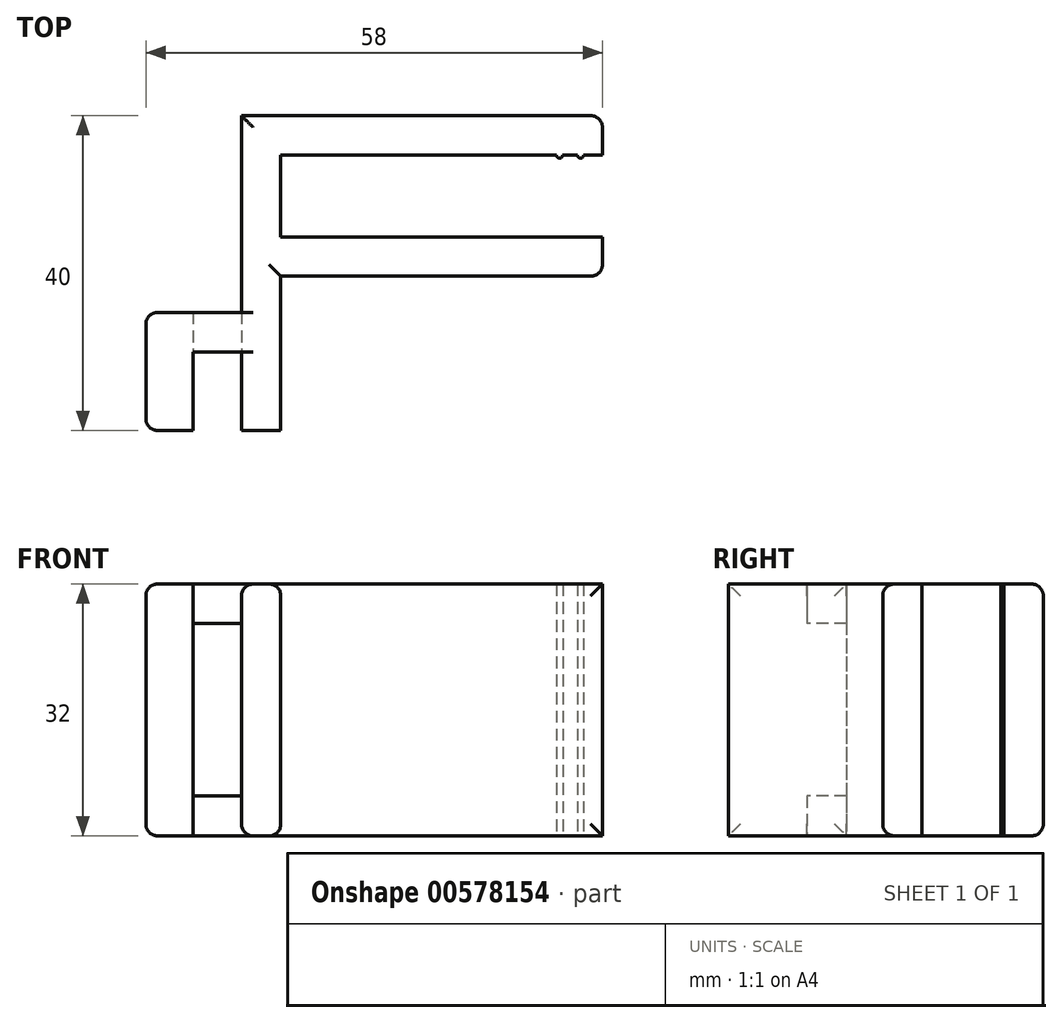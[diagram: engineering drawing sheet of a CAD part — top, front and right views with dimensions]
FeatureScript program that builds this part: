
annotation { "Feature Type Name" : "Feature", "Feature Type Description" : "" }
export const myFeature = defineFeature(function(context is Context, id is Id, definition is map)
    precondition{}
    {
        {
            var Q0;
            Q0=qCreatedBy(makeId("Top.planeOp"),FACE);
            var sketch = newSketch(context, id + "F0", { "sketchPlane" : qUnion([Q0])});
            skLineSegment(sketch, "E0.bottom", {"start": v(0, 0) * mm, "end": v(6, 0) * mm});
            skLineSegment(sketch, "E0.top", {"start": v(12.14, 40) * mm, "end": v(58, 40) * mm});
            skLineSegment(sketch, "E0.left", {"start": v(0, 0) * mm, "end": v(0, 15) * mm});
            skLineSegment(sketch, "E0.right", {"start": v(58, 25) * mm, "end": v(58, 30) * mm});
            skLineSegment(sketch, "E1", {"start": v(58, 35) * mm, "end": v(17.14, 35) * mm});
            skLineSegment(sketch, "E2", {"start": v(58, 25) * mm, "end": v(17.14, 25) * mm});
            skLineSegment(sketch, "E3", {"start": v(6, 0) * mm, "end": v(6, 15) * mm});
            skLineSegment(sketch, "E4", {"start": v(12.14, 0) * mm, "end": v(12.14, 25) * mm});
            skLineSegment(sketch, "E5", {"start": v(17.14, 0) * mm, "end": v(17.14, 25) * mm});
            skLineSegment(sketch, "E6", {"start": v(6, 10) * mm, "end": v(12.14, 10) * mm});
            skLineSegment(sketch, "E7", {"start": v(0, 15) * mm, "end": v(12.14, 15) * mm});
            skLineSegment(sketch, "E8", {"start": v(17.14, 30) * mm, "end": v(17.14, 35) * mm});
            skLineSegment(sketch, "E9", {"start": v(12.14, 25) * mm, "end": v(12.14, 40) * mm});
            skLineSegment(sketch, "E10.trimOffspring", {"start": v(12.14, 0) * mm, "end": v(17.14, 0) * mm});
            skLineSegment(sketch, "E11.trimOffspring", {"start": v(17.14, 30) * mm, "end": v(58, 30) * mm});
            skPoint(sketch, "E12.start.orphan", {"position": v(0, 30) * mm});
            skPoint(sketch, "E13.start.orphan", {"position": v(60.37, 35) * mm});
            skPoint(sketch, "E14.end.orphan", {"position": v(60.37, 40) * mm});
            skPoint(sketch, "E15.start.orphan", {"position": v(60.37, 30) * mm});
            skLineSegment(sketch, "E16.trimOffspring", {"start": v(58, 35) * mm, "end": v(58, 40) * mm});
            skArc(sketch, "E17", {"start": v(52.16, 35) * mm, "mid": v(52.56, 34.6) * mm, "end": v(52.96, 35) * mm});
            skArc(sketch, "E18", {"start": v(54.82, 35) * mm, "mid": v(55.22, 34.6) * mm, "end": v(55.62, 35) * mm});
            skSolve(sketch);
        }
        {
            var Q0;
            Q0 = qSketchRegion(id + "F0", true);
            extrude(context, id + "F1", {"entities" : qUnion([Q0]), "depth" : 32 * mm, "offsetDistance" : 25 * mm});
        }
        {
            var Q0;
            Q0=makeQuery(id+"F1.opExtrude","SWEPT_FACE",FACE,{"disambiguationData":[OSD([sQuery(id+"F0.wireOp",EDGE,"E6")])]});
            var sketch = newSketch(context, id + "F2", { "sketchPlane" : qUnion([Q0])});
            skLineSegment(sketch, "E19.bottom", {"start": v(6, 0) * mm, "end": v(12.14, 0) * mm});
            skLineSegment(sketch, "E19.top", {"start": v(6, 5.07) * mm, "end": v(12.14, 5.07) * mm});
            skLineSegment(sketch, "E19.left", {"start": v(6, 0) * mm, "end": v(6, 5.07) * mm});
            skLineSegment(sketch, "E19.right", {"start": v(12.14, 0) * mm, "end": v(12.14, 5.07) * mm});
            skLineSegment(sketch, "E20.bottom", {"start": v(6, 32) * mm, "end": v(12.14, 32) * mm});
            skLineSegment(sketch, "E20.top", {"start": v(6, 27) * mm, "end": v(12.14, 27) * mm});
            skLineSegment(sketch, "E20.left", {"start": v(6, 32) * mm, "end": v(6, 27) * mm});
            skLineSegment(sketch, "E20.right", {"start": v(12.14, 32) * mm, "end": v(12.14, 27) * mm});
            skSolve(sketch);
        }
        {
            var Q0;
            {var subQ0=sQuery(id+"F2.wireOp",EDGE,"E19.top");Q0=makeQuery(id+"F2.imprint","IMPRINT",FACE,{"disambiguationData":[TD([[makeQuery(id+"F2.imprint","IMPRINT",EDGE,{"derivedFrom":subQ0}),1.0]])]});}
            extrude(context, id + "F3", {"entities" : qUnion([Q0]), "operationType" : NewBodyOperationType.REMOVE, "oppositeDirection" : true, "depth" : 5 * mm, "offsetDistance" : 25 * mm});
        }
        {
            var Q0;
            Q0=makeQuery(id+"F1.opExtrude","SWEPT_FACE",FACE,{"disambiguationData":[OSD([sQuery(id+"F0.wireOp",EDGE,"E2")])]});
            extrude(context, id + "F4", {"entities" : qUnion([Q0]), "operationType" : NewBodyOperationType.ADD, "depth" : 5.4 * mm, "offsetDistance" : 25 * mm});
        }
        {
            var Q0;
            Q0=makeQuery(id+"F1.opExtrude","SWEPT_FACE",FACE,{"disambiguationData":[OSD([sQuery(id+"F0.wireOp",EDGE,"E11.trimOffspring")])]});
            extrude(context, id + "F5", {"entities" : qUnion([Q0]), "operationType" : NewBodyOperationType.REMOVE, "oppositeDirection" : true, "depth" : 5.4 * mm, "offsetDistance" : 25 * mm});
        }
        {
            var Q0;
            Q0=makeQuery(id+"F1.opExtrude","CAP_EDGE",EDGE,{"disambiguationData":[OSD([sQuery(id+"F0.wireOp",EDGE,"E4"),sQuery(id+"F0.wireOp",EDGE,"E9")])],"isStart":false});
            var Q1;
            Q1=makeQuery(id+"F1.opExtrude","CAP_EDGE",EDGE,{"disambiguationData":[OSD([sQuery(id+"F0.wireOp",EDGE,"E4"),sQuery(id+"F0.wireOp",EDGE,"E9")])],"isStart":true});
            var Q2;
            Q2=makeQuery(id+"F1.opExtrude","CAP_EDGE",EDGE,{"disambiguationData":[OSD([sQuery(id+"F0.wireOp",EDGE,"E4")])],"isStart":true});
            var Q3;
            Q3=makeQuery(id+"F1.opExtrude","SWEPT_FACE",FACE,{"disambiguationData":[OSD([sQuery(id+"F0.wireOp",EDGE,"E0.left")])]});
            var Q4;
            Q4=makeQuery(id+"F1.opExtrude","CAP_EDGE",EDGE,{"disambiguationData":[OSD([sQuery(id+"F0.wireOp",EDGE,"E4")])],"isStart":false});
            var Q5;
            Q5=makeQuery(id+"F1.opExtrude","CAP_EDGE",EDGE,{"disambiguationData":[OSD([sQuery(id+"F0.wireOp",EDGE,"E5")])],"isStart":true});
            var Q6;
            {var subQ0=sQuery(id+"F0.wireOp",EDGE,"E11.trimOffspring");var subQ1=sQuery(id+"F0.wireOp",EDGE,"E8");Q6=makeQuery(id+"F5.boolean.opBoolean","MERGE",EDGE,{"derivedFrom":[makeQuery(id+"F1.opExtrude","CAP_EDGE",EDGE,{"disambiguationData":[OSD([subQ1])],"isStart":true}),makeQuery(id+"F5.opExtrude","SWEPT_EDGE",EDGE,{"disambiguationData":[OSD([subQ1,subQ0]),TDD([makeQuery(id+"F1.opExtrude","CAP_VERTEX",VERTEX,{"disambiguationData":[OSD([subQ1,subQ0])],"isStart":true})])]})]});}
            var Q7;
            {var subQ0=sQuery(id+"F0.wireOp",EDGE,"E11.trimOffspring");var subQ1=sQuery(id+"F0.wireOp",EDGE,"E8");Q7=makeQuery(id+"F5.boolean.opBoolean","MERGE",EDGE,{"derivedFrom":[makeQuery(id+"F1.opExtrude","CAP_EDGE",EDGE,{"disambiguationData":[OSD([subQ1])],"isStart":false}),makeQuery(id+"F5.opExtrude","SWEPT_EDGE",EDGE,{"disambiguationData":[OSD([subQ1,subQ0]),TDD([makeQuery(id+"F1.opExtrude","CAP_VERTEX",VERTEX,{"disambiguationData":[OSD([subQ1,subQ0])],"isStart":false})])]})]});}
            var Q8;
            Q8=makeQuery(id+"F1.opExtrude","CAP_EDGE",EDGE,{"disambiguationData":[OSD([sQuery(id+"F0.wireOp",EDGE,"E5")])],"isStart":false});
            var Q9;
            {var subQ0=sQuery(id+"F0.wireOp",EDGE,"E2");Q9=makeQuery(id+"F4.opExtrude","CAP_EDGE",EDGE,{"disambiguationData":[OSD([subQ0]),TDD([makeQuery(id+"F1.opExtrude","CAP_EDGE",EDGE,{"disambiguationData":[OSD([subQ0])],"isStart":false})])],"isStart":false});}
            var Q10;
            {var subQ0=sQuery(id+"F0.wireOp",EDGE,"E2");Q10=makeQuery(id+"F4.opExtrude","CAP_EDGE",EDGE,{"disambiguationData":[OSD([subQ0]),TDD([makeQuery(id+"F1.opExtrude","CAP_EDGE",EDGE,{"disambiguationData":[OSD([subQ0])],"isStart":true})])],"isStart":false});}
            var Q11;
            Q11=makeQuery(id+"F1.opExtrude","CAP_EDGE",EDGE,{"disambiguationData":[OSD([sQuery(id+"F0.wireOp",EDGE,"E0.top")])],"isStart":true});
            var Q12;
            Q12=makeQuery(id+"F1.opExtrude","CAP_EDGE",EDGE,{"disambiguationData":[OSD([sQuery(id+"F0.wireOp",EDGE,"E0.top")])],"isStart":false});
            var Q13;
            Q13=makeQuery(id+"F1.opExtrude","SWEPT_EDGE",EDGE,{"disambiguationData":[OSD([sQuery(id+"F0.wireOp",EDGE,"E0.top"),sQuery(id+"F0.wireOp",EDGE,"E16.trimOffspring")])]});
            var Q14;
            Q14=makeQuery(id+"F4.opExtrude","CAP_EDGE",EDGE,{"disambiguationData":[OSD([sQuery(id+"F0.wireOp",EDGE,"E0.right"),sQuery(id+"F0.wireOp",EDGE,"E2")])],"isStart":false});
            fillet(context, id + "F6", {"entities" : qUnion([Q0, Q1, Q2, Q3, Q4, Q5, Q6, Q7, Q8, Q9, Q10, Q11, Q12, Q13, Q14]), "radius" : 1.5 * mm, "tangentPropagation" : true, "allowEdgeOverflow" : false});
        }
    });
